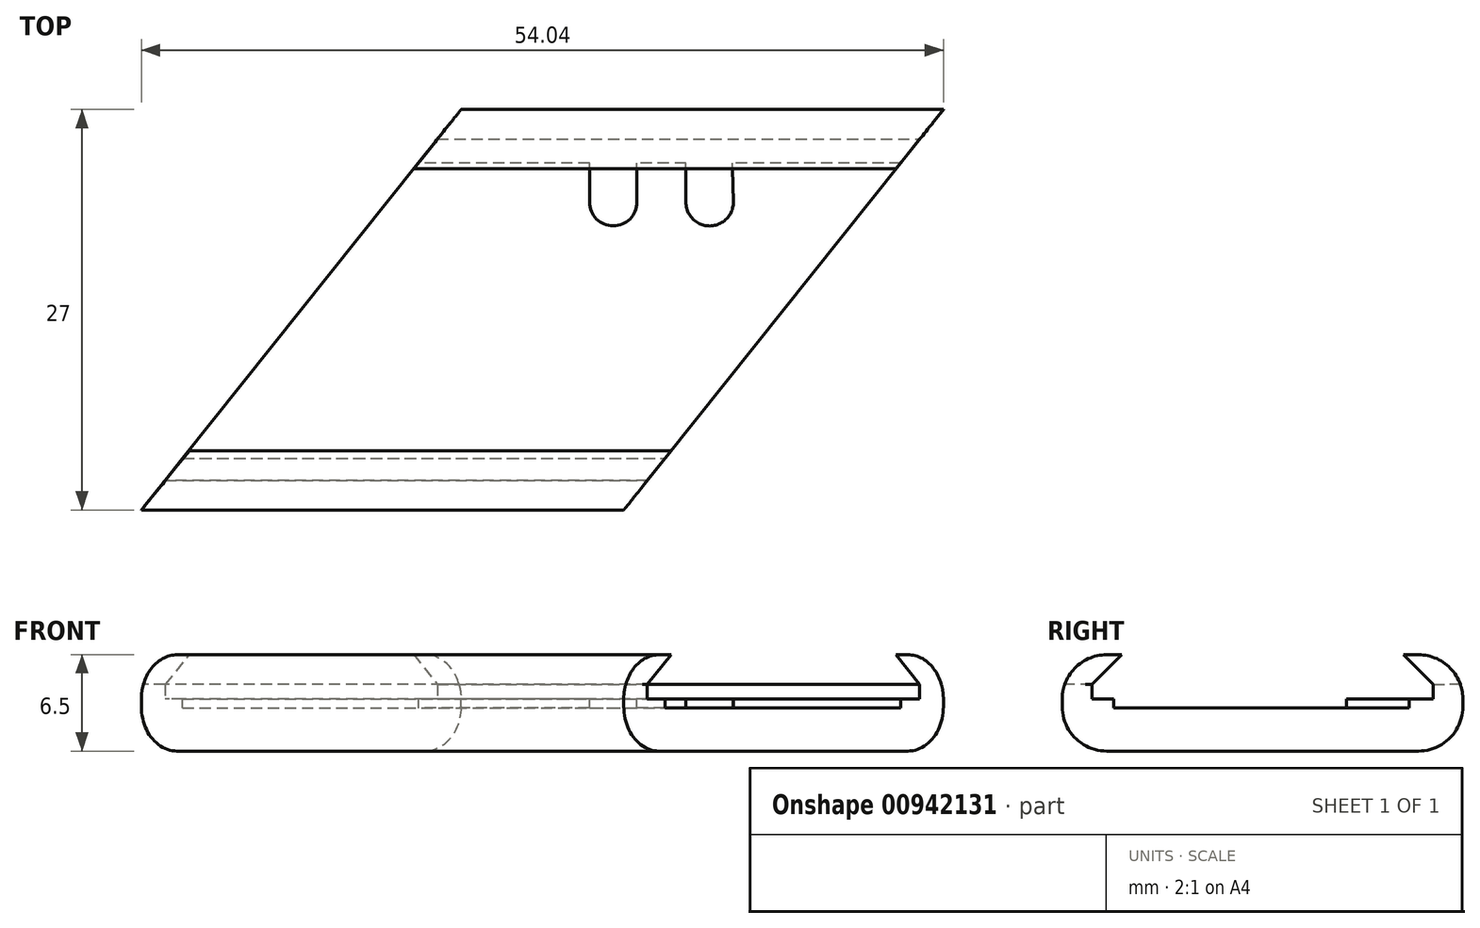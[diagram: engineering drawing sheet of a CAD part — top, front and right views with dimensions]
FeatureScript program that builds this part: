
annotation { "Feature Type Name" : "Feature", "Feature Type Description" : "" }
export const myFeature = defineFeature(function(context is Context, id is Id, definition is map)
    precondition{}
    {
        {
            var Q0;
            Q0=qCreatedBy(makeId("Top.planeOp"),FACE);
            var sketch = newSketch(context, id + "F0", { "sketchPlane" : qUnion([Q0])});
            skLineSegment(sketch, "E0", {"start": v(-31, -19) * mm, "end": v(31, -19) * mm});
            skLineSegment(sketch, "E1", {"start": v(31, -19) * mm, "end": v(31, 0) * mm, "construction": true});
            skLineSegment(sketch, "E2", {"start": v(31, 0) * mm, "end": v(-31, 0) * mm});
            skLineSegment(sketch, "E3", {"start": v(-16, 0) * mm, "end": v(16, 0) * mm});
            skPoint(sketch, "E4", {"position": v(0, 0) * mm});
            skLineSegment(sketch, "E5", {"start": v(16, 0) * mm, "end": v(31, -19) * mm});
            skLineSegment(sketch, "E6", {"start": v(-16, 0) * mm, "end": v(-31, -19) * mm});
            skLineSegment(sketch, "E7", {"start": v(-3.25, 0) * mm, "end": v(3.25, 0) * mm, "construction": true});
            skLineSegment(sketch, "E8", {"start": v(-3.25, 0) * mm, "end": v(-3.25, -4) * mm, "construction": true});
            skLineSegment(sketch, "E9", {"start": v(3.25, 0) * mm, "end": v(3.25, -4) * mm, "construction": true});
            skCircle(sketch, "E10", {"center": v(-3.25, -2.25) * mm, "radius": 1.75 * mm});
            skLineSegment(sketch, "E11", {"start": v(-5, -2.19) * mm, "end": v(-5, 0) * mm});
            skLineSegment(sketch, "E12", {"start": v(-1.5, -2.2) * mm, "end": v(-1.5, 0) * mm});
            skLineSegment(sketch, "E13", {"start": v(-3.25, -2.25) * mm, "end": v(3.25, -2.25) * mm, "construction": true});
            skCircle(sketch, "E14", {"center": v(3.25, -2.25) * mm, "radius": 1.75 * mm});
            skLineSegment(sketch, "E15", {"start": v(1.5, -2.25) * mm, "end": v(1.5, 0) * mm});
            skLineSegment(sketch, "E16", {"start": v(5, -2.25) * mm, "end": v(5, 0) * mm});
            skSolve(sketch);
        }
        {
            var Q0;
            Q0=qCreatedBy(makeId("Top.planeOp"),FACE);
            var sketch = newSketch(context, id + "F1", { "sketchPlane" : qUnion([Q0])});
            skLineSegment(sketch, "E17", {"start": v(-16.98, 0) * mm, "end": v(-32.75, -19.52) * mm});
            skLineSegment(sketch, "E18", {"start": v(-32.75, -19.52) * mm, "end": v(32.33, -19.52) * mm});
            skLineSegment(sketch, "E19", {"start": v(32.33, -19.52) * mm, "end": v(16.46, 0.4) * mm});
            skLineSegment(sketch, "E20", {"start": v(16.46, 0.4) * mm, "end": v(-16.68, 0.4) * mm});
            skLineSegment(sketch, "E21", {"start": v(-16.68, 0.4) * mm, "end": v(-16.98, 0) * mm});
            skCircle(sketch, "E22", {"center": v(-3.24, -2.24) * mm, "radius": 1.6 * mm});
            skCircle(sketch, "E23", {"center": v(3.25, -2.25) * mm, "radius": 1.6 * mm});
            skLineSegment(sketch, "E24", {"start": v(-3.24, -2.24) * mm, "end": v(3.25, -2.25) * mm, "construction": true});
            skLineSegment(sketch, "E25", {"start": v(-4.84, -2.24) * mm, "end": v(-4.84, 0.4) * mm});
            skLineSegment(sketch, "E26", {"start": v(-1.64, -2.24) * mm, "end": v(-1.64, 0.4) * mm});
            skLineSegment(sketch, "E27", {"start": v(1.65, -2.25) * mm, "end": v(1.65, 0.4) * mm});
            skLineSegment(sketch, "E28", {"start": v(4.85, -2.21) * mm, "end": v(4.8, 0.4) * mm});
            skSolve(sketch);
        }
        {
            var Q0;
            Q0=qCreatedBy(makeId("Top.planeOp"),FACE);
            var sketch = newSketch(context, id + "F2", { "sketchPlane" : qUnion([Q0])});
            skLineSegment(sketch, "E29", {"start": v(19, 4) * mm, "end": v(-13.5, 4) * mm});
            skLineSegment(sketch, "E30", {"start": v(-13.5, 4) * mm, "end": v(-35.04, -23) * mm});
            skLineSegment(sketch, "E31", {"start": v(-35.04, -23) * mm, "end": v(-2.54, -23) * mm});
            skLineSegment(sketch, "E32", {"start": v(19, 4) * mm, "end": v(-2.54, -23) * mm});
            skSolve(sketch);
        }
        {
            var Q0;
            Q0=makeQuery(id+"F2.imprint","IMPRINT",FACE,{"disambiguationData":[TD([[makeQuery(id+"F2.imprint","IMPRINT",EDGE,{"derivedFrom":sQuery(id+"F2.wireOp",EDGE,"E29")}),1.0]])]});
            extrude(context, id + "F3", {"entities" : qUnion([Q0]), "oppositeDirection" : true, "depth" : 3.5 * mm, "offsetDistance" : 25 * mm});
        }
        {
            var Q0;
            Q0=makeQuery(id+"F1.imprint","IMPRINT",FACE,{"disambiguationData":[TD([[makeQuery(id+"F1.imprint","IMPRINT",EDGE,{"derivedFrom":sQuery(id+"F1.wireOp",EDGE,"E17")}),1.0]])]});
            extrude(context, id + "F4", {"entities" : qUnion([Q0]), "operationType" : NewBodyOperationType.REMOVE, "oppositeDirection" : true, "depth" : 0.6 * mm, "offsetDistance" : 25 * mm});
        }
        {
            var Q0;
            Q0=makeQuery(id+"F3.opExtrude","CAP_FACE",FACE,{"disambiguationData":[OSD([sQuery(id+"F2.wireOp",EDGE,"E29"),sQuery(id+"F2.wireOp",EDGE,"E30"),sQuery(id+"F2.wireOp",EDGE,"E31"),sQuery(id+"F2.wireOp",EDGE,"E32")])],"isStart":true});
            var sketch = newSketch(context, id + "F5", { "sketchPlane" : qUnion([Q0])});
            skLineSegment(sketch, "E33", {"start": v(19, 4) * mm, "end": v(-13.5, 4) * mm});
            skLineSegment(sketch, "E34", {"start": v(-13.5, 4) * mm, "end": v(-15.1, 2) * mm});
            skLineSegment(sketch, "E35", {"start": v(-15.1, 2) * mm, "end": v(17.4, 2) * mm});
            skLineSegment(sketch, "E36", {"start": v(17.4, 2) * mm, "end": v(19, 4) * mm});
            skLineSegment(sketch, "E37", {"start": v(-35.04, -23) * mm, "end": v(-2.54, -23) * mm});
            skLineSegment(sketch, "E38", {"start": v(-2.54, -23) * mm, "end": v(-0.94, -21) * mm});
            skLineSegment(sketch, "E39", {"start": v(-0.94, -21) * mm, "end": v(-33.44, -21) * mm});
            skLineSegment(sketch, "E40", {"start": v(-33.44, -21) * mm, "end": v(-35.04, -23) * mm});
            skSolve(sketch);
        }
        {
            var Q0;
            Q0=makeQuery(id+"F5.imprint","IMPRINT",FACE,{"disambiguationData":[TD([[makeQuery(id+"F5.imprint","IMPRINT",EDGE,{"derivedFrom":sQuery(id+"F5.wireOp",EDGE,"E37")}),1.0]])]});
            var Q1;
            Q1=makeQuery(id+"F5.imprint","IMPRINT",FACE,{"disambiguationData":[TD([[makeQuery(id+"F5.imprint","IMPRINT",EDGE,{"derivedFrom":sQuery(id+"F5.wireOp",EDGE,"E33")}),1.0]])]});
            extrude(context, id + "F6", {"entities" : qUnion([Q0, Q1]), "operationType" : NewBodyOperationType.ADD, "depth" : 1 * mm, "offsetDistance" : 25 * mm});
        }
        {
            var Q0;
            Q0=makeQuery(id+"F6.opExtrude","CAP_FACE",FACE,{"disambiguationData":[OSD([sQuery(id+"F5.wireOp",EDGE,"E33"),sQuery(id+"F5.wireOp",EDGE,"E34"),sQuery(id+"F5.wireOp",EDGE,"E35"),sQuery(id+"F5.wireOp",EDGE,"E36")])],"isStart":false});
            var sketch = newSketch(context, id + "F7", { "sketchPlane" : qUnion([Q0])});
            skLineSegment(sketch, "E41", {"start": v(19, 4) * mm, "end": v(-13.5, 4) * mm});
            skLineSegment(sketch, "E42", {"start": v(-13.5, 4) * mm, "end": v(-16.69, 0) * mm});
            skLineSegment(sketch, "E43", {"start": v(-16.69, 0) * mm, "end": v(15.8, 0) * mm});
            skLineSegment(sketch, "E44", {"start": v(15.8, 0) * mm, "end": v(19, 4) * mm});
            skLineSegment(sketch, "E45", {"start": v(-35.04, -23) * mm, "end": v(-2.54, -23) * mm});
            skLineSegment(sketch, "E46", {"start": v(-2.54, -23) * mm, "end": v(0.65, -19) * mm});
            skLineSegment(sketch, "E47", {"start": v(0.65, -19) * mm, "end": v(-31.79, -19) * mm});
            skLineSegment(sketch, "E48", {"start": v(-31.79, -19) * mm, "end": v(-35.04, -23) * mm});
            skSolve(sketch);
        }
        {
            var Q0;
            Q0 = qSketchRegion(id + "F7", true);
            extrude(context, id + "F8", {"entities" : qUnion([Q0]), "operationType" : NewBodyOperationType.ADD, "depth" : 2 * mm, "offsetDistance" : 25 * mm});
        }
        {
            var Q0;
            Q0=makeQuery(id+"F8.opExtrude","CAP_EDGE",EDGE,{"disambiguationData":[OSD([sQuery(id+"F7.wireOp",EDGE,"E43")])],"isStart":true});
            var Q1;
            Q1=makeQuery(id+"F8.opExtrude","CAP_EDGE",EDGE,{"disambiguationData":[OSD([sQuery(id+"F7.wireOp",EDGE,"E47")])],"isStart":true});
            chamfer(context, id + "F9", {"entities" : qUnion([Q0, Q1]), "width" : 2 * mm, "tangentPropagation" : true});
        }
        {
            var Q0;
            Q0=makeQuery(id+"F8.opExtrude","CAP_EDGE",EDGE,{"disambiguationData":[OSD([sQuery(id+"F7.wireOp",EDGE,"E45")])],"isStart":false});
            var Q1;
            Q1=makeQuery(id+"F3.opExtrude","CAP_EDGE",EDGE,{"disambiguationData":[OSD([sQuery(id+"F2.wireOp",EDGE,"E31")])],"isStart":false});
            var Q2;
            Q2=makeQuery(id+"F3.opExtrude","CAP_EDGE",EDGE,{"disambiguationData":[OSD([sQuery(id+"F2.wireOp",EDGE,"E29")])],"isStart":false});
            var Q3;
            Q3=makeQuery(id+"F8.opExtrude","CAP_EDGE",EDGE,{"disambiguationData":[OSD([sQuery(id+"F7.wireOp",EDGE,"E41")])],"isStart":false});
            fillet(context, id + "F10", {"entities" : qUnion([Q0, Q1, Q2, Q3]), "radius" : 3 * mm, "tangentPropagation" : true, "allowEdgeOverflow" : false});
        }
    });
